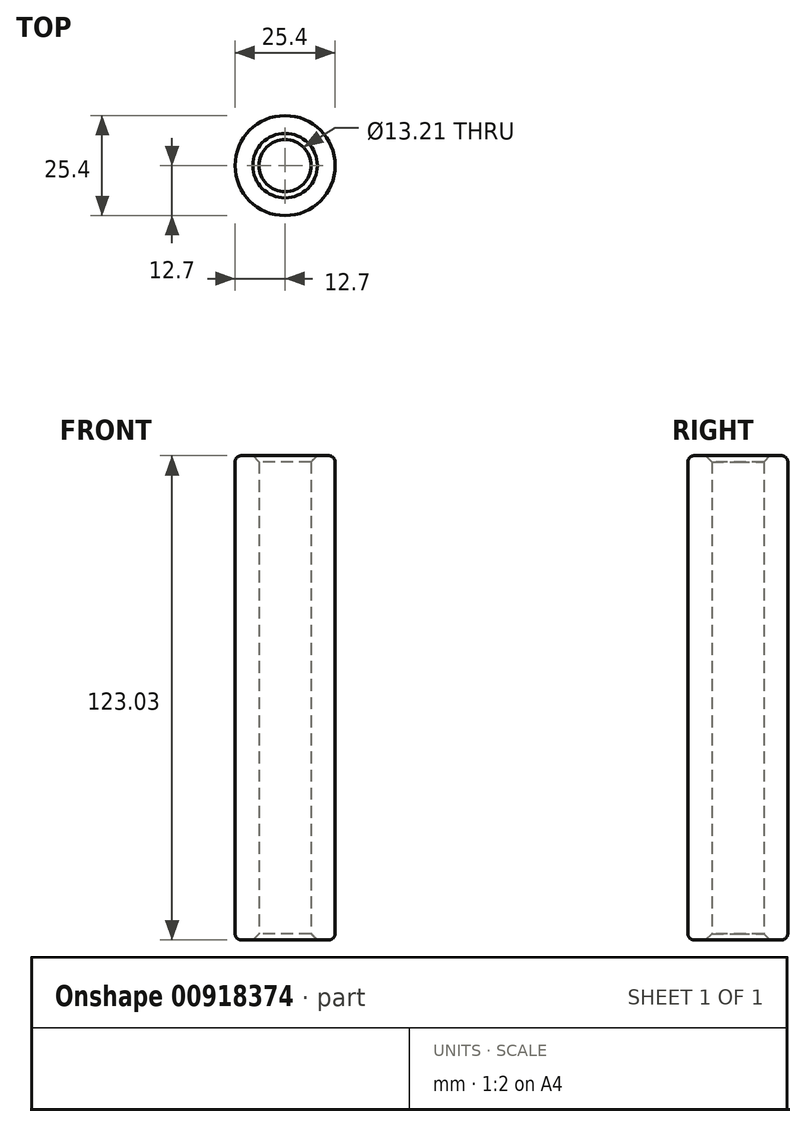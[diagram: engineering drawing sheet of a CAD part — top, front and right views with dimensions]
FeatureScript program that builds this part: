
annotation { "Feature Type Name" : "Feature", "Feature Type Description" : "" }
export const myFeature = defineFeature(function(context is Context, id is Id, definition is map)
    precondition{}
    {
        {
            var Q0;
            Q0=qCreatedBy(makeId("Top.planeOp"),FACE);
            var sketch = newSketch(context, id + "F0", { "sketchPlane" : qUnion([Q0])});
            skCircle(sketch, "E0", {"center": v(0, 0) * mm, "radius": 12.7 * mm});
            skCircle(sketch, "E1", {"center": v(0, 0) * mm, "radius": 6.6 * mm});
            skSolve(sketch);
        }
        {
            var Q0;
            Q0=makeQuery(id+"F0.imprint","IMPRINT",FACE,{"disambiguationData":[TD([[makeQuery(id+"F0.imprint","IMPRINT",EDGE,{"derivedFrom":sQuery(id+"F0.wireOp",EDGE,"E0")}),1.0]])]});
            extrude(context, id + "F1", {"entities" : qUnion([Q0]), "depth" : 123.03 * mm, "offsetDistance" : 25.4 * mm});
        }
        {
            var Q0;
            Q0=makeQuery(id+"F1.opExtrude","SWEPT_FACE",FACE,{"disambiguationData":[OSD([sQuery(id+"F0.wireOp",EDGE,"E1")])]});
            chamfer(context, id + "F2", {"entities" : qUnion([Q0]), "width" : 1.59 * mm, "tangentPropagation" : true});
        }
        {
            var Q0;
            Q0=makeQuery(id+"F1.opExtrude","SWEPT_FACE",FACE,{"disambiguationData":[OSD([sQuery(id+"F0.wireOp",EDGE,"E0")])]});
            fillet(context, id + "F3", {"entities" : qUnion([Q0]), "radius" : 1.59 * mm, "tangentPropagation" : true, "allowEdgeOverflow" : false});
        }
    });
